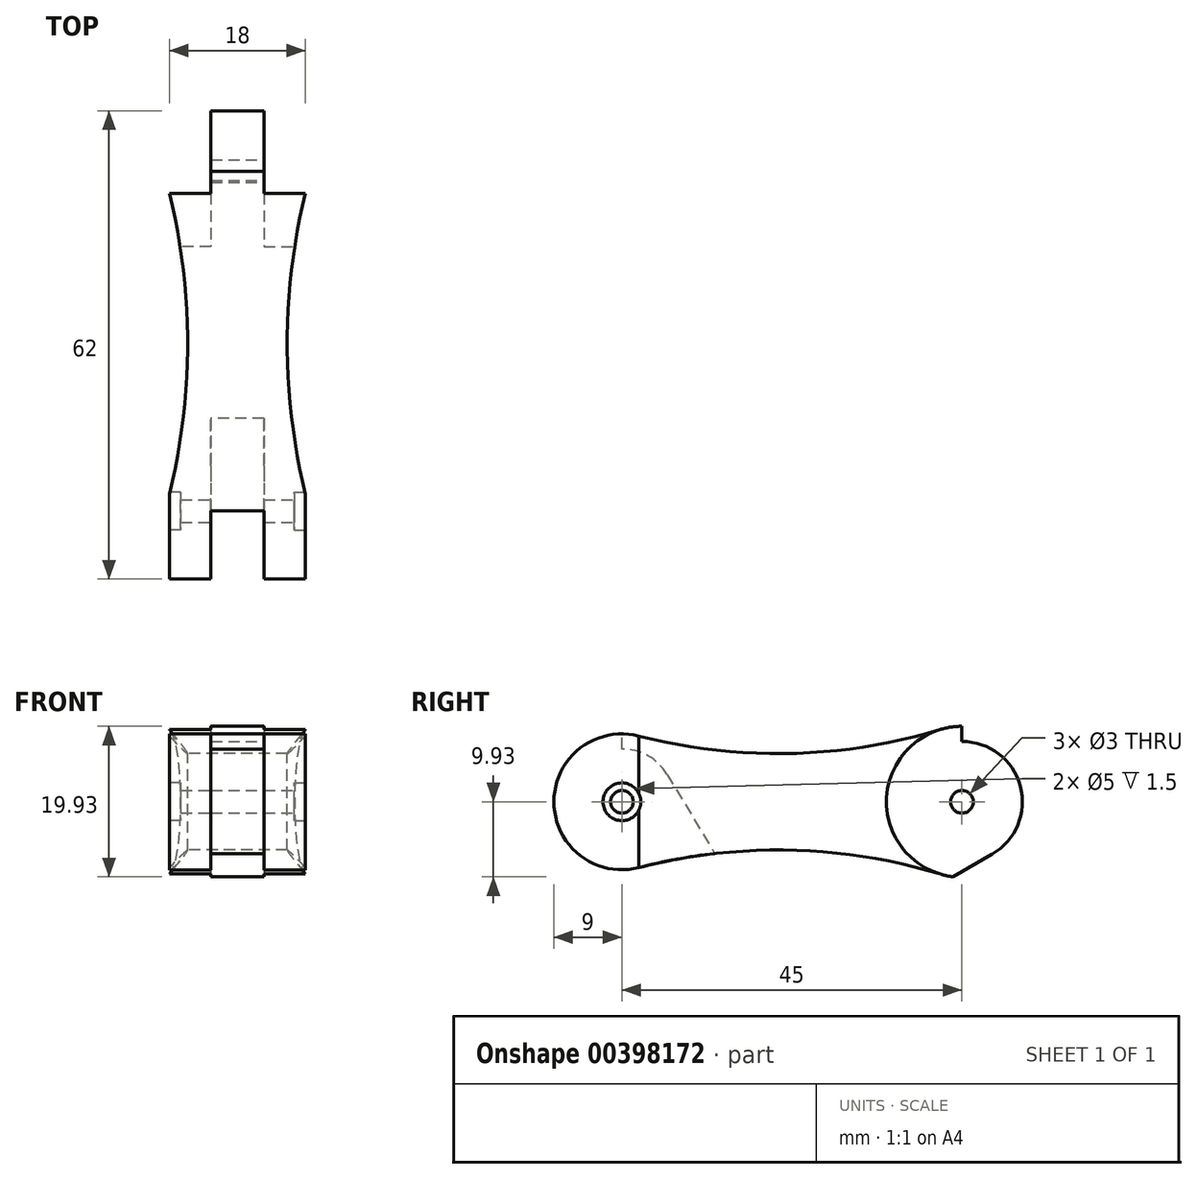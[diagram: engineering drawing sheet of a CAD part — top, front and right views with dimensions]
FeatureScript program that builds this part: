
annotation { "Feature Type Name" : "Feature", "Feature Type Description" : "" }
export const myFeature = defineFeature(function(context is Context, id is Id, definition is map)
    precondition{}
    {
        {
            var Q0;
            Q0=qCreatedBy(makeId("Right.planeOp"),FACE);
            var sketch = newSketch(context, id + "F0", { "sketchPlane" : qUnion([Q0])});
            skArc(sketch, "E0", {"start": v(2.25, 8.71) * mm, "mid": v(-9, 0) * mm, "end": v(2.25, -8.71) * mm});
            skLineSegment(sketch, "E1", {"start": v(-29.92, 0) * mm, "end": v(87.26, 0) * mm, "construction": true});
            skArc(sketch, "E2", {"start": v(42.09, -9.57) * mm, "mid": v(55, 0) * mm, "end": v(42.09, 9.57) * mm});
            skArc(sketch, "E3", {"start": v(2.25, 8.71) * mm, "mid": v(22.23, 6.4) * mm, "end": v(42.09, 9.57) * mm});
            skArc(sketch, "E4", {"start": v(42.09, -9.57) * mm, "mid": v(22.23, -6.4) * mm, "end": v(2.25, -8.71) * mm});
            skSolve(sketch);
        }
        {
            var Q0;
            Q0=qSketchRegion(id+"F0",true);
            extrude(context, id + "F1", {"entities" : qUnion([Q0]), "depth" : 5.5 * mm});
        }
        {
            var Q0;
            Q0=makeQuery(id+"F1.opExtrude","CAP_FACE",FACE,{"disambiguationData":[OSD([sQuery(id+"F0.wireOp",EDGE,"E0"),sQuery(id+"F0.wireOp",EDGE,"E2"),sQuery(id+"F0.wireOp",EDGE,"E3"),sQuery(id+"F0.wireOp",EDGE,"E4")])],"isStart":false});
            var sketch = newSketch(context, id + "F2", { "sketchPlane" : qUnion([Q0])});
            skArc(sketch, "E5.0", {"start": v(2.25, 8.71) * mm, "mid": v(22.23, 6.4) * mm, "end": v(42.09, 9.57) * mm});
            skArc(sketch, "E6.0", {"start": v(2.25, 8.71) * mm, "mid": v(1.13, 8.93) * mm, "end": v(0, 9) * mm});
            skArc(sketch, "E7.0", {"start": v(42.09, -9.57) * mm, "mid": v(27.33, -6.68) * mm, "end": v(12.29, -6.85) * mm});
            skArc(sketch, "E8.0", {"start": v(42.09, -9.57) * mm, "mid": v(55, 0) * mm, "end": v(42.09, 9.57) * mm});
            skArc(sketch, "E9", {"start": v(6, 3.6) * mm, "mid": v(3.45, 6.1) * mm, "end": v(0, 7) * mm});
            skLineSegment(sketch, "E10", {"start": v(0, 7) * mm, "end": v(0, 9) * mm});
            skLineSegment(sketch, "E11", {"start": v(0, 0) * mm, "end": v(34.92, 0) * mm, "construction": true});
            skLineSegment(sketch, "E12", {"start": v(6, 3.6) * mm, "end": v(12.29, -6.85) * mm});
            skPoint(sketch, "E13.orphan", {"position": v(7, 0) * mm});
            skSolve(sketch);
        }
        {
            var Q0;
            Q0=qSketchRegion(id+"F2",true);
            extrude(context, id + "F3", {"entities" : qUnion([Q0]), "operationType" : NewBodyOperationType.ADD, "depth" : 7 * mm});
        }
        {
            var Q0;
            Q0=makeQuery(id+"F3.opExtrude","CAP_FACE",FACE,{"disambiguationData":[OSD([sQuery(id+"F2.wireOp",EDGE,"E5.0"),sQuery(id+"F2.wireOp",EDGE,"E6.0"),sQuery(id+"F2.wireOp",EDGE,"E7.0"),sQuery(id+"F2.wireOp",EDGE,"E8.0"),sQuery(id+"F2.wireOp",EDGE,"E9"),sQuery(id+"F2.wireOp",EDGE,"E10"),sQuery(id+"F2.wireOp",EDGE,"JRJ70NO1-7vJe-Li3z-EIXT-plhISmGAnEbH")])],"isStart":false});
            var sketch = newSketch(context, id + "F4", { "sketchPlane" : qUnion([Q0])});
            skArc(sketch, "E14.0", {"start": v(0, 9) * mm, "mid": v(-8.93, -1.13) * mm, "end": v(2.25, -8.71) * mm});
            skArc(sketch, "E15.0", {"start": v(2.25, 8.71) * mm, "mid": v(22.23, 6.4) * mm, "end": v(42.09, 9.57) * mm});
            skArc(sketch, "E16.0", {"start": v(12.29, -6.85) * mm, "mid": v(7.24, -7.61) * mm, "end": v(2.25, -8.71) * mm});
            skArc(sketch, "E17.0", {"start": v(42.09, -9.57) * mm, "mid": v(27.33, -6.68) * mm, "end": v(12.29, -6.85) * mm});
            skArc(sketch, "E18.0", {"start": v(42.09, -9.57) * mm, "mid": v(55, 0) * mm, "end": v(42.09, 9.57) * mm});
            skArc(sketch, "E19.0", {"start": v(2.25, 8.71) * mm, "mid": v(1.13, 8.93) * mm, "end": v(0, 9) * mm});
            skSolve(sketch);
        }
        {
            var Q0;
            Q0=qSketchRegion(id+"F4",true);
            extrude(context, id + "F5", {"entities" : qUnion([Q0]), "operationType" : NewBodyOperationType.ADD, "depth" : 5.5 * mm});
        }
        {
            var Q0;
            Q0=makeQuery(id+"F5.opExtrude","CAP_FACE",FACE,{"disambiguationData":[OSD([sQuery(id+"F4.wireOp",EDGE,"E14.0"),sQuery(id+"F4.wireOp",EDGE,"E15.0"),sQuery(id+"F4.wireOp",EDGE,"E16.0"),sQuery(id+"F4.wireOp",EDGE,"E17.0"),sQuery(id+"F4.wireOp",EDGE,"E18.0"),sQuery(id+"F4.wireOp",EDGE,"E19.0")])],"isStart":false});
            var sketch = newSketch(context, id + "F6", { "sketchPlane" : qUnion([Q0])});
            skCircle(sketch, "E20", {"center": v(45, 0) * mm, "radius": 10 * mm});
            skSolve(sketch);
        }
        {
            var Q0;
            Q0=qSketchRegion(id+"F6",true);
            extrude(context, id + "F7", {"entities" : qUnion([Q0]), "operationType" : NewBodyOperationType.REMOVE, "oppositeDirection" : true, "depth" : 5.5 * mm});
        }
        {
            var Q0;
            Q0=makeQuery(id+"F1.opExtrude","CAP_FACE",FACE,{"disambiguationData":[OSD([sQuery(id+"F0.wireOp",EDGE,"E0"),sQuery(id+"F0.wireOp",EDGE,"E2"),sQuery(id+"F0.wireOp",EDGE,"E3"),sQuery(id+"F0.wireOp",EDGE,"E4")])],"isStart":true});
            var sketch = newSketch(context, id + "F8", { "sketchPlane" : qUnion([Q0])});
            skCircle(sketch, "E21", {"center": v(-45, 0) * mm, "radius": 10 * mm});
            skSolve(sketch);
        }
        {
            var Q0;
            Q0=qSketchRegion(id+"F8",true);
            extrude(context, id + "F9", {"entities" : qUnion([Q0]), "operationType" : NewBodyOperationType.REMOVE, "oppositeDirection" : true, "depth" : 5.5 * mm});
        }
        {
            var Q0;
            Q0=makeQuery(id+"F7.boolean.opBoolean","COPY",FACE,{"derivedFrom":makeQuery(id+"F7.opExtrude","CAP_FACE",FACE,{"disambiguationData":[OSD([sQuery(id+"F6.wireOp",EDGE,"E20")])],"isStart":false})});
            var sketch = newSketch(context, id + "F10", { "sketchPlane" : qUnion([Q0])});
            skArc(sketch, "E22", {"start": v(49, -6.93) * mm, "mid": v(52.73, 2.07) * mm, "end": v(45, 8) * mm});
            skLineSegment(sketch, "E23", {"start": v(45, 10) * mm, "end": v(45, 8) * mm});
            skArc(sketch, "E24", {"start": v(43.8, -9.93) * mm, "mid": v(54.98, -0.6) * mm, "end": v(45, 10) * mm});
            skLineSegment(sketch, "E25", {"start": v(49, -6.93) * mm, "end": v(43.8, -9.93) * mm});
            skSolve(sketch);
        }
        {
            var Q0;
            Q0=qSketchRegion(id+"F10",true);
            extrude(context, id + "F11", {"entities" : qUnion([Q0]), "operationType" : NewBodyOperationType.REMOVE, "endBound" : BoundingType.THROUGH_ALL, "oppositeDirection" : true, "depth" : 25 * mm});
        }
        {
            var Q0;
            Q0=makeQuery(id+"F5.opExtrude","CAP_FACE",FACE,{"disambiguationData":[OSD([sQuery(id+"F4.wireOp",EDGE,"E14.0"),sQuery(id+"F4.wireOp",EDGE,"E15.0"),sQuery(id+"F4.wireOp",EDGE,"E16.0"),sQuery(id+"F4.wireOp",EDGE,"E18.0"),sQuery(id+"F4.wireOp",EDGE,"E19.0"),sQuery(id+"F4.wireOp",EDGE,"E17.0")])],"isStart":false});
            var sketch = newSketch(context, id + "F12", { "sketchPlane" : qUnion([Q0])});
            skCircle(sketch, "E26", {"center": v(0, 0) * mm, "radius": 1.5 * mm});
            skCircle(sketch, "E27", {"center": v(45, 0) * mm, "radius": 1.5 * mm});
            skSolve(sketch);
        }
        {
            var Q0;
            Q0=qSketchRegion(id+"F12",true);
            extrude(context, id + "F13", {"entities" : qUnion([Q0]), "operationType" : NewBodyOperationType.REMOVE, "endBound" : BoundingType.THROUGH_ALL, "oppositeDirection" : true, "depth" : 25 * mm});
        }
        {
            var Q0;
            Q0=makeQuery(id+"F5.opExtrude","CAP_FACE",FACE,{"disambiguationData":[OSD([sQuery(id+"F4.wireOp",EDGE,"E14.0"),sQuery(id+"F4.wireOp",EDGE,"E15.0"),sQuery(id+"F4.wireOp",EDGE,"E16.0"),sQuery(id+"F4.wireOp",EDGE,"E18.0"),sQuery(id+"F4.wireOp",EDGE,"E19.0"),sQuery(id+"F4.wireOp",EDGE,"E17.0")])],"isStart":false});
            var sketch = newSketch(context, id + "F14", { "sketchPlane" : qUnion([Q0])});
            skCircle(sketch, "E28", {"center": v(0, 0) * mm, "radius": 2.5 * mm});
            skSolve(sketch);
        }
        {
            var Q0;
            Q0=qSketchRegion(id+"F14",true);
            extrude(context, id + "F15", {"entities" : qUnion([Q0]), "operationType" : NewBodyOperationType.REMOVE, "oppositeDirection" : true, "depth" : 1.5 * mm});
        }
        {
            var Q0;
            Q0=makeQuery(id+"F1.opExtrude","CAP_FACE",FACE,{"disambiguationData":[OSD([sQuery(id+"F0.wireOp",EDGE,"E0"),sQuery(id+"F0.wireOp",EDGE,"E2"),sQuery(id+"F0.wireOp",EDGE,"E3"),sQuery(id+"F0.wireOp",EDGE,"E4")])],"isStart":true});
            var sketch = newSketch(context, id + "F16", { "sketchPlane" : qUnion([Q0])});
            skCircle(sketch, "E29", {"center": v(0, 0) * mm, "radius": 2.5 * mm});
            skSolve(sketch);
        }
        {
            var Q0;
            Q0=qSketchRegion(id+"F16",true);
            extrude(context, id + "F17", {"entities" : qUnion([Q0]), "operationType" : NewBodyOperationType.REMOVE, "oppositeDirection" : true, "depth" : 1.5 * mm});
        }
        {
            var Q0;
            Q0=qCreatedBy(makeId("Top.planeOp"),FACE);
            var sketch = newSketch(context, id + "F18", { "sketchPlane" : qUnion([Q0])});
            skCircle(sketch, "E30", {"center": v(-81, 22.17) * mm, "radius": 83.41 * mm});
            skCircle(sketch, "E31", {"center": v(99, 22.17) * mm, "radius": 83.41 * mm});
            skSolve(sketch);
        }
        {
            var Q0;
            Q0=qSketchRegion(id+"F18",true);
            extrude(context, id + "F19", {"entities" : qUnion([Q0]), "operationType" : NewBodyOperationType.REMOVE, "endBound" : BoundingType.SYMMETRIC, "oppositeDirection" : true, "depth" : 25 * mm});
        }
    });
